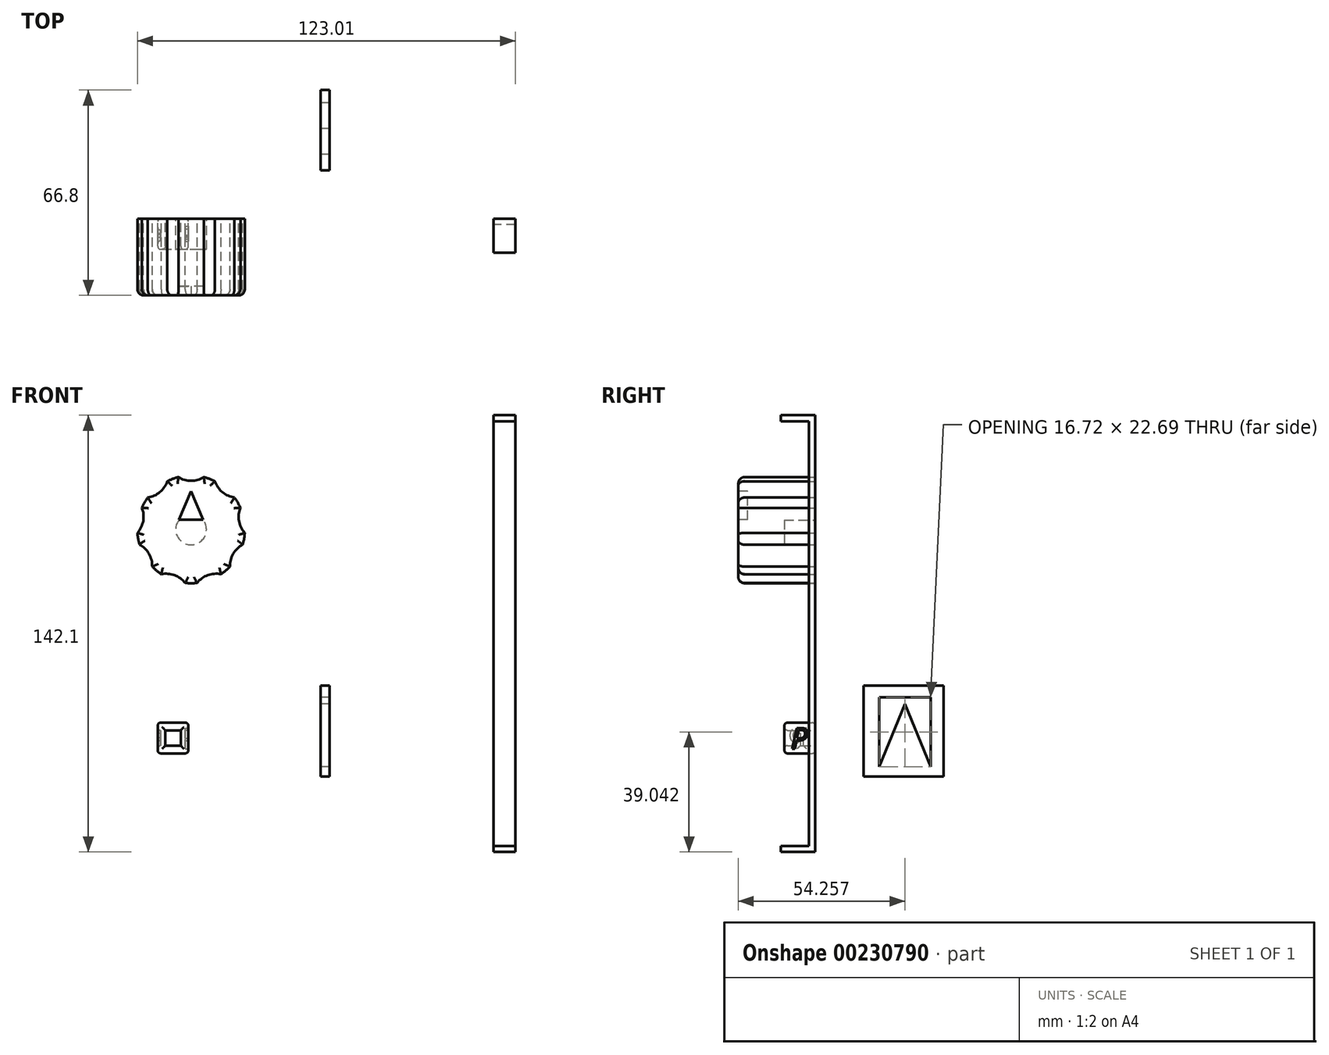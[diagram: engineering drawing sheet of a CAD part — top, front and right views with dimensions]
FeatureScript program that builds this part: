
annotation { "Feature Type Name" : "Feature", "Feature Type Description" : "" }
export const myFeature = defineFeature(function(context is Context, id is Id, definition is map)
    precondition{}
    {
        {
            var Q0;
            Q0=qCreatedBy(makeId("Right.planeOp"),FACE);
            var sketch = newSketch(context, id + "F0", { "sketchPlane" : qUnion([Q0])});
            skLineSegment(sketch, "E0", {"start": v(15.72, -16.12) * mm, "end": v(15.72, -45.78) * mm});
            skLineSegment(sketch, "E1", {"start": v(15.72, -45.78) * mm, "end": v(41.8, -45.78) * mm});
            skLineSegment(sketch, "E2", {"start": v(41.8, -45.78) * mm, "end": v(41.8, -16.12) * mm});
            skLineSegment(sketch, "E3", {"start": v(41.8, -16.12) * mm, "end": v(15.72, -16.12) * mm});
            skLineSegment(sketch, "E4", {"start": v(20.9, -19.9) * mm, "end": v(20.9, -42.6) * mm});
            skLineSegment(sketch, "E5", {"start": v(20.9, -42.6) * mm, "end": v(29.26, -22.1) * mm});
            skLineSegment(sketch, "E6", {"start": v(29.26, -22.1) * mm, "end": v(37.62, -42.6) * mm});
            skLineSegment(sketch, "E7", {"start": v(37.62, -42.6) * mm, "end": v(37.62, -19.9) * mm});
            skLineSegment(sketch, "E8", {"start": v(37.62, -19.9) * mm, "end": v(20.9, -19.9) * mm});
            skSolve(sketch);
        }
        {
            var Q0;
            Q0=makeQuery(id+"F0.imprint","IMPRINT",FACE,{"disambiguationData":[TD([[makeQuery(id+"F0.imprint","IMPRINT",EDGE,{"derivedFrom":sQuery(id+"F0.wireOp",EDGE,"E0")}),1.0]])]});
            extrude(context, id + "F1", {"entities" : qUnion([Q0]), "depth" : 3 * mm});
        }
        {
            var Q0;
            Q0=qCreatedBy(makeId("Front.planeOp"),FACE);
            var sketch = newSketch(context, id + "F2", { "sketchPlane" : qUnion([Q0])});
            skCircle(sketch, "E9", {"center": v(-42.1, 34.67) * mm, "radius": 17.5 * mm});
            skCircle(sketch, "E10", {"center": v(-42.1, 34.67) * mm, "radius": 5 * mm});
            skLineSegment(sketch, "E11", {"start": v(-46.1, 37.67) * mm, "end": v(-38.1, 37.67) * mm});
            skLineSegment(sketch, "E12", {"start": v(-46.22, 51.67) * mm, "end": v(-37.97, 51.67) * mm, "construction": true});
            skArc(sketch, "E13", {"start": v(-46.22, 51.67) * mm, "mid": v(-42.1, 50.5) * mm, "end": v(-37.97, 51.67) * mm});
            skArc(sketch, "E14.1.0", {"start": v(-56.19, 45.04) * mm, "mid": v(-52.27, 46.8) * mm, "end": v(-49.87, 50.34) * mm});
            skArc(sketch, "E14.2.0", {"start": v(-59.56, 33.56) * mm, "mid": v(-57.68, 37.41) * mm, "end": v(-58.13, 41.68) * mm});
            skArc(sketch, "E14.3.0", {"start": v(-54.76, 22.6) * mm, "mid": v(-55.8, 26.75) * mm, "end": v(-58.88, 29.73) * mm});
            skArc(sketch, "E14.4.0", {"start": v(-44.04, 17.27) * mm, "mid": v(-47.5, 19.8) * mm, "end": v(-51.79, 20.1) * mm});
            skArc(sketch, "E14.5.0", {"start": v(-32.4, 20.1) * mm, "mid": v(-36.68, 19.8) * mm, "end": v(-40.15, 17.27) * mm});
            skArc(sketch, "E14.6.0", {"start": v(-25.3, 29.73) * mm, "mid": v(-28.39, 26.75) * mm, "end": v(-29.43, 22.6) * mm});
            skArc(sketch, "E14.7.0", {"start": v(-26.06, 41.68) * mm, "mid": v(-26.5, 37.41) * mm, "end": v(-24.63, 33.56) * mm});
            skArc(sketch, "E14.8.0", {"start": v(-34.32, 50.34) * mm, "mid": v(-31.92, 46.8) * mm, "end": v(-28, 45.04) * mm});
            skSolve(sketch);
        }
        {
            var Q0;
            {var subQ9=sQuery(id+"F2.wireOp",EDGE,"E13");Q0=makeQuery(id+"F2.imprint","IMPRINT",FACE,{"disambiguationData":[TD([[makeQuery(id+"F2.imprint","IMPRINT",EDGE,{"derivedFrom":subQ9}),-1.0]])]});}
            var Q1;
            {var subQ0=sQuery(id+"F2.wireOp",EDGE,"E11");Q1=makeQuery(id+"F2.imprint","IMPRINT",FACE,{"disambiguationData":[TD([[makeQuery(id+"F2.imprint","IMPRINT",EDGE,{"derivedFrom":subQ0}),1.0]])]});}
            var Q2;
            {var subQ0=sQuery(id+"F2.wireOp",EDGE,"E11");Q2=makeQuery(id+"F2.imprint","IMPRINT",FACE,{"disambiguationData":[TD([[makeQuery(id+"F2.imprint","IMPRINT",EDGE,{"derivedFrom":subQ0}),-1.0]])]});}
            extrude(context, id + "F3", {"entities" : qUnion([Q0, Q1, Q2]), "depth" : 25 * mm});
        }
        {
            var Q0;
            {var subQ0=sQuery(id+"F2.wireOp",EDGE,"E11");Q0=makeQuery(id+"F2.imprint","IMPRINT",FACE,{"disambiguationData":[TD([[makeQuery(id+"F2.imprint","IMPRINT",EDGE,{"derivedFrom":subQ0}),-1.0]])]});}
            extrude(context, id + "F4", {"entities" : qUnion([Q0]), "operationType" : NewBodyOperationType.REMOVE, "depth" : 10 * mm});
        }
        {
            var Q0;
            Q0=makeQuery(id+"F3.opExtrude","CAP_FACE",FACE,{"disambiguationData":[OSD([sQuery(id+"F2.wireOp",EDGE,"E9"),sQuery(id+"F2.wireOp",EDGE,"E13"),sQuery(id+"F2.wireOp",EDGE,"E14.1.0"),sQuery(id+"F2.wireOp",EDGE,"E14.2.0"),sQuery(id+"F2.wireOp",EDGE,"E14.3.0"),sQuery(id+"F2.wireOp",EDGE,"E14.4.0"),sQuery(id+"F2.wireOp",EDGE,"E14.5.0"),sQuery(id+"F2.wireOp",EDGE,"E14.6.0"),sQuery(id+"F2.wireOp",EDGE,"E14.7.0"),sQuery(id+"F2.wireOp",EDGE,"E14.8.0")])],"isStart":false});
            fillet(context, id + "F5", {"entities" : qUnion([Q0]), "radius" : 2 * mm, "tangentPropagation" : true, "allowEdgeOverflow" : false});
        }
        {
            var Q0;
            Q0=makeQuery(id+"F3.opExtrude","CAP_FACE",FACE,{"disambiguationData":[OSD([sQuery(id+"F2.wireOp",EDGE,"E9"),sQuery(id+"F2.wireOp",EDGE,"E13"),sQuery(id+"F2.wireOp",EDGE,"E14.1.0"),sQuery(id+"F2.wireOp",EDGE,"E14.2.0"),sQuery(id+"F2.wireOp",EDGE,"E14.3.0"),sQuery(id+"F2.wireOp",EDGE,"E14.4.0"),sQuery(id+"F2.wireOp",EDGE,"E14.5.0"),sQuery(id+"F2.wireOp",EDGE,"E14.6.0"),sQuery(id+"F2.wireOp",EDGE,"E14.7.0"),sQuery(id+"F2.wireOp",EDGE,"E14.8.0")])],"isStart":false});
            var sketch = newSketch(context, id + "F6", { "sketchPlane" : qUnion([Q0])});
            skLineSegment(sketch, "E15", {"start": v(-42.1, 48.5) * mm, "end": v(-42.1, 27) * mm, "construction": true});
            skLineSegment(sketch, "E16", {"start": v(-38.17, 37.84) * mm, "end": v(-42.1, 37.84) * mm});
            skLineSegment(sketch, "E17.MirrorCS", {"start": v(-46.02, 37.84) * mm, "end": v(-42.1, 37.84) * mm});
            skLineSegment(sketch, "E18", {"start": v(-46.02, 37.84) * mm, "end": v(-42.1, 47.08) * mm});
            skLineSegment(sketch, "E19.MirrorCS", {"start": v(-38.17, 37.84) * mm, "end": v(-42.1, 47.08) * mm});
            skSolve(sketch);
        }
        {
            var Q0;
            Q0=makeQuery(id+"F6.imprint","IMPRINT",FACE,{"disambiguationData":[TD([[makeQuery(id+"F6.imprint","IMPRINT",EDGE,{"derivedFrom":sQuery(id+"F6.wireOp",EDGE,"E16")}),-1.0]])]});
            extrude(context, id + "F7", {"entities" : qUnion([Q0]), "operationType" : NewBodyOperationType.REMOVE, "oppositeDirection" : true, "depth" : 3 * mm});
        }
        {
            var Q0;
            Q0=qCreatedBy(makeId("Front.planeOp"),FACE);
            var sketch = newSketch(context, id + "F8", { "sketchPlane" : qUnion([Q0])});
            skLineSegment(sketch, "E20", {"start": v(63.45, -70.29) * mm, "end": v(63.45, 71.81) * mm});
            skLineSegment(sketch, "E21", {"start": v(56.35, 71.81) * mm, "end": v(56.35, -70.29) * mm});
            skLineSegment(sketch, "E22", {"start": v(63.45, 71.81) * mm, "end": v(56.35, 71.81) * mm});
            skLineSegment(sketch, "E23", {"start": v(56.35, -70.29) * mm, "end": v(63.45, -70.29) * mm});
            skLineSegment(sketch, "E24", {"start": v(56.35, 69.81) * mm, "end": v(63.45, 69.81) * mm});
            skLineSegment(sketch, "E25", {"start": v(63.45, 69.81) * mm, "end": v(63.45, 71.81) * mm});
            skLineSegment(sketch, "E26", {"start": v(56.35, 71.81) * mm, "end": v(56.35, 69.81) * mm});
            skLineSegment(sketch, "E27", {"start": v(56.35, -70.29) * mm, "end": v(56.35, -68.29) * mm});
            skLineSegment(sketch, "E28", {"start": v(56.35, -68.29) * mm, "end": v(63.45, -68.29) * mm});
            skLineSegment(sketch, "E29", {"start": v(63.45, -68.29) * mm, "end": v(63.45, -70.29) * mm});
            skSolve(sketch);
        }
        {
            var Q0;
            Q0=makeQuery(id+"F8.imprint","IMPRINT",FACE,{"disambiguationData":[TD([[makeQuery(id+"F8.imprint","IMPRINT",EDGE,{"derivedFrom":sQuery(id+"F8.wireOp",EDGE,"E20")}),1.0]])]});
            extrude(context, id + "F9", {"entities" : qUnion([Q0]), "depth" : 2 * mm});
        }
        {
            var Q0;
            Q0=makeQuery(id+"F8.imprint","IMPRINT",FACE,{"disambiguationData":[TD([[makeQuery(id+"F8.imprint","IMPRINT",EDGE,{"derivedFrom":sQuery(id+"F8.wireOp",EDGE,"E22")}),1.0]])]});
            extrude(context, id + "F10", {"entities" : qUnion([Q0]), "operationType" : NewBodyOperationType.ADD, "depth" : 11.1 * mm});
        }
        {
            var Q0;
            Q0=makeQuery(id+"F8.imprint","IMPRINT",FACE,{"disambiguationData":[TD([[makeQuery(id+"F8.imprint","IMPRINT",EDGE,{"derivedFrom":sQuery(id+"F8.wireOp",EDGE,"E23")}),1.0]])]});
            extrude(context, id + "F11", {"entities" : qUnion([Q0]), "operationType" : NewBodyOperationType.ADD, "depth" : 11.1 * mm});
        }
        {
            var Q0;
            Q0=qCreatedBy(makeId("Front.planeOp"),FACE);
            var sketch = newSketch(context, id + "F12", { "sketchPlane" : qUnion([Q0])});
            skLineSegment(sketch, "E30.bottom", {"start": v(-52.98, -28.2) * mm, "end": v(-42.98, -28.2) * mm});
            skLineSegment(sketch, "E30.top", {"start": v(-52.98, -38.2) * mm, "end": v(-42.98, -38.2) * mm});
            skLineSegment(sketch, "E30.left", {"start": v(-52.98, -28.2) * mm, "end": v(-52.98, -38.2) * mm});
            skLineSegment(sketch, "E30.right", {"start": v(-42.98, -28.2) * mm, "end": v(-42.98, -38.2) * mm});
            skLineSegment(sketch, "E31.bottom", {"start": v(-50.48, -30.7) * mm, "end": v(-45.48, -30.7) * mm});
            skLineSegment(sketch, "E31.top", {"start": v(-50.48, -35.7) * mm, "end": v(-45.48, -35.7) * mm});
            skLineSegment(sketch, "E31.left", {"start": v(-50.48, -30.7) * mm, "end": v(-50.48, -35.7) * mm});
            skLineSegment(sketch, "E31.right", {"start": v(-45.48, -30.7) * mm, "end": v(-45.48, -35.7) * mm});
            skSolve(sketch);
        }
        {
            var Q0;
            Q0=makeQuery(id+"F12.imprint","IMPRINT",FACE,{"disambiguationData":[TD([[makeQuery(id+"F12.imprint","IMPRINT",EDGE,{"derivedFrom":sQuery(id+"F12.wireOp",EDGE,"E30.bottom")}),-1.0]])]});
            extrude(context, id + "F13", {"entities" : qUnion([Q0]), "depth" : 10 * mm});
        }
        {
            var Q0;
            Q0=makeQuery(id+"F12.imprint","IMPRINT",FACE,{"disambiguationData":[TD([[makeQuery(id+"F12.imprint","IMPRINT",EDGE,{"derivedFrom":sQuery(id+"F12.wireOp",EDGE,"E31.bottom")}),-1.0]])]});
            extrude(context, id + "F14", {"entities" : qUnion([Q0]), "operationType" : NewBodyOperationType.REMOVE, "depth" : 2.5 * mm});
        }
        {
            var Q0;
            Q0=makeQuery(id+"F13.opExtrude","SWEPT_FACE",FACE,{"disambiguationData":[OSD([sQuery(id+"F12.wireOp",EDGE,"E30.left")])]});
            var sketch = newSketch(context, id + "F15", { "sketchPlane" : qUnion([Q0])});
            skText(sketch, "E32", { "text": "P", "fontName": "OpenSans-Bold.ttf"});
            const initialGuessF15  = {"E32": [0.0032, -0.0357, 1, 0, 0.00496]};
            skSetInitialGuess(sketch, initialGuessF15);
            skSolve(sketch);
        }
        {
            var Q0;
            Q0=makeQuery(id+"F15.imprint","IMPRINT",FACE,{"disambiguationData":[TD([[makeQuery(id+"F15.imprint","IMPRINT",EDGE,{"derivedFrom":sQuery(id+"F15.wireOp",EDGE,"E32.sketch_text.stroke-0")}),-1.0]])]});
            extrude(context, id + "F16", {"entities" : qUnion([Q0]), "operationType" : NewBodyOperationType.REMOVE, "oppositeDirection" : true, "depth" : 1 * mm});
        }
        {
            var Q0;
            Q0=makeQuery(id+"F13.opExtrude","SWEPT_FACE",FACE,{"disambiguationData":[OSD([sQuery(id+"F12.wireOp",EDGE,"E30.right")])]});
            fillet(context, id + "F17", {"entities" : qUnion([Q0]), "radius" : 1 * mm, "tangentPropagation" : true, "allowEdgeOverflow" : false});
        }
        {
            var Q0;
            Q0=makeQuery(id+"F13.opExtrude","SWEPT_FACE",FACE,{"disambiguationData":[OSD([sQuery(id+"F12.wireOp",EDGE,"E30.top")])]});
            fillet(context, id + "F18", {"entities" : qUnion([Q0]), "radius" : 1 * mm, "tangentPropagation" : true, "allowEdgeOverflow" : false});
        }
        {
            var Q0;
            {var subQ0=sQuery(id+"F12.wireOp",EDGE,"E30.bottom");var subQ6=sQuery(id+"F12.wireOp",EDGE,"E30.left");Q0=makeQuery(id+"F16.boolean.opBoolean","SPLIT",FACE,{"disambiguationData":[TD([makeQuery(id+"F13.opExtrude","SWEPT_FACE",FACE,{"disambiguationData":[OSD([subQ0])]})])],"derivedFrom":makeQuery(id+"F13.opExtrude","SWEPT_FACE",FACE,{"disambiguationData":[OSD([subQ6])]})});}
            fillet(context, id + "F19", {"entities" : qUnion([Q0]), "radius" : 1 * mm, "tangentPropagation" : true, "allowEdgeOverflow" : false});
        }
        {
            var Q0;
            Q0=makeQuery(id+"F13.opExtrude","CAP_FACE",FACE,{"disambiguationData":[OSD([sQuery(id+"F12.wireOp",EDGE,"E30.bottom"),sQuery(id+"F12.wireOp",EDGE,"E30.top"),sQuery(id+"F12.wireOp",EDGE,"E30.left"),sQuery(id+"F12.wireOp",EDGE,"E30.right"),sQuery(id+"F12.wireOp",EDGE,"E31.bottom"),sQuery(id+"F12.wireOp",EDGE,"E31.top"),sQuery(id+"F12.wireOp",EDGE,"E31.left"),sQuery(id+"F12.wireOp",EDGE,"E31.right")])],"isStart":false});
            var Q1;
            Q1=makeQuery(id+"F13.opExtrude","SWEPT_FACE",FACE,{"disambiguationData":[OSD([sQuery(id+"F12.wireOp",EDGE,"E30.bottom")])]});
            fillet(context, id + "F20", {"entities" : qUnion([Q0, Q1]), "radius" : 1 * mm, "tangentPropagation" : true, "allowEdgeOverflow" : false});
        }
        {
            var Q0;
            Q0=makeQuery(id+"F13.opExtrude","SWEPT_FACE",FACE,{"disambiguationData":[OSD([sQuery(id+"F12.wireOp",EDGE,"E30.right")])]});
            var sketch = newSketch(context, id + "F21", { "sketchPlane" : qUnion([Q0])});
            skText(sketch, "E33", { "text": "P", "fontName": "OpenSans-Italic.ttf"});
            const initialGuessF21  = {"E33": [-0.00783, -0.03667, 1, 0, 0.0068]};
            skSetInitialGuess(sketch, initialGuessF21);
            skSolve(sketch);
        }
        {
            var Q0;
            Q0 = qSketchRegion(id + "F21", true);
            extrude(context, id + "F22", {"entities" : qUnion([Q0]), "operationType" : NewBodyOperationType.REMOVE, "oppositeDirection" : true, "depth" : 1 * mm});
        }
    });
